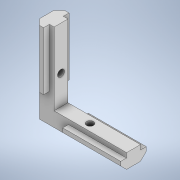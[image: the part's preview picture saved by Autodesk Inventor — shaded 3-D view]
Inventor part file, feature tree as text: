
AUTODESK INVENTOR PART (.ipt)
format: ipt  version: 2020 (Build 240168000, 168)  size: 161,280 bytes
history: native  units: mm
features: extrude x6, sketch x6
ambient origin geometry x8: Origin, YZ Plane, XZ Plane, XY Plane, X Axis, Y Axis, Z Axis, Center Point
bodies: Solide1 (feature_tree)
feature tree (12):
  extrude  "Extrusion1"  Depth=3.0mm
  extrude  "Extrusion2"  Depth=3.0mm
  extrude  "Extrusion3"  Depth=1.75mm
  extrude  "Extrusion4"  Depth=1.75mm
  extrude  "Extrusion5"  Depth=2.0mm
  extrude  "Extrusion6"  Depth=25.0mm TaperAngle=0.0deg
  sketch  "Esquisse1"
  sketch  "Esquisse2"
  sketch  "Esquisse3"
  sketch  "Esquisse4"
  sketch  "Esquisse6"
  sketch  "Esquisse7"
